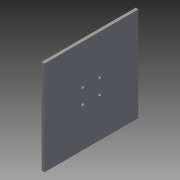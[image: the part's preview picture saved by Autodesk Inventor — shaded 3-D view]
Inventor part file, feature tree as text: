
AUTODESK INVENTOR PART (.ipt)
format: ipt  version: 2014 (Build 180170000, 170)  size: 79,360 bytes
history: native  units: mm
features: extrude x2, sketch x2
ambient origin geometry x8: Origin, YZ Plane, XZ Plane, XY Plane, X Axis, Y Axis, Z Axis, Center Point
bodies: Solid1 (feature_tree)
feature tree (4):
  extrude  "Extrusion1"  Depth=100.0mm
  extrude  "Extrusion2"  Depth=3.0mm TaperAngle=0.0deg
  sketch  "Sketch1"  dims[d0=100.0mm d1=100.0mm]
  sketch  "Sketch2"  dims[d2=3.0mm d3=0.0mm d4=3.0mm d5=0.0mm]
